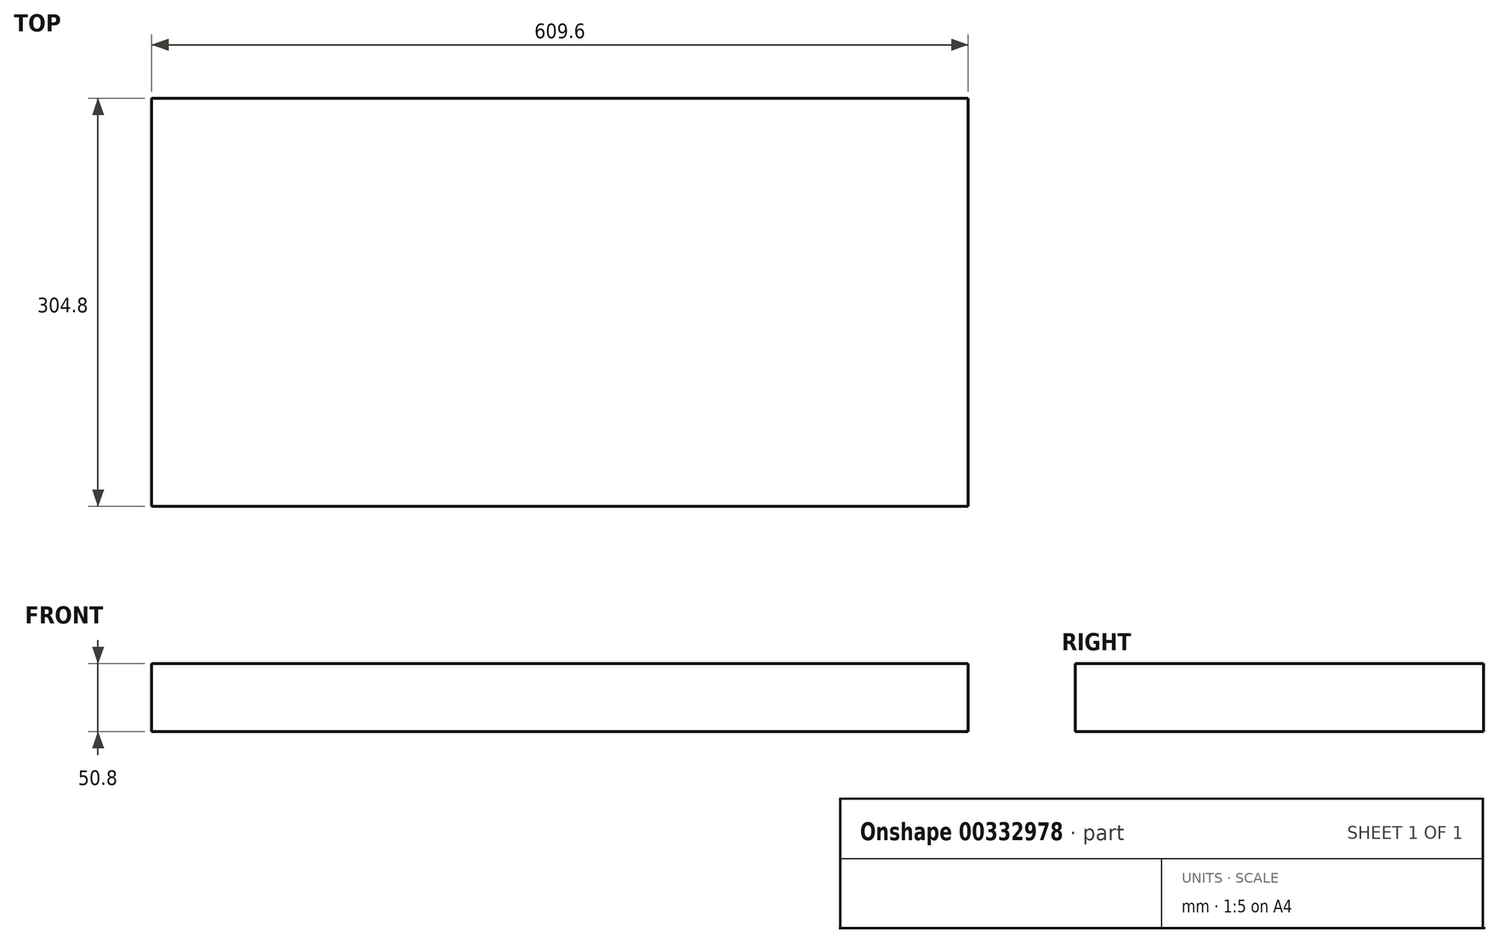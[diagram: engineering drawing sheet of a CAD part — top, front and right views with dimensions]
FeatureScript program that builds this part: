
annotation { "Feature Type Name" : "Feature", "Feature Type Description" : "" }
export const myFeature = defineFeature(function(context is Context, id is Id, definition is map)
    precondition{}
    {
        {
            var Q0;
            Q0=qCreatedBy(makeId("Top.planeOp"),FACE);
            var sketch = newSketch(context, id + "F0", { "sketchPlane" : qUnion([Q0])});
            skLineSegment(sketch, "E0.bottom", {"start": v(304.8, -152.4) * mm, "end": v(-304.8, -152.4) * mm});
            skLineSegment(sketch, "E0.top", {"start": v(304.8, 152.4) * mm, "end": v(-304.8, 152.4) * mm});
            skLineSegment(sketch, "E0.left", {"start": v(304.8, -152.4) * mm, "end": v(304.8, 152.4) * mm});
            skLineSegment(sketch, "E0.right", {"start": v(-304.8, -152.4) * mm, "end": v(-304.8, 152.4) * mm});
            skPoint(sketch, "E0.middle", {"position": v(0, 0) * mm});
            skSolve(sketch);
        }
        {
            var Q0;
            Q0 = qSketchRegion(id + "F0", true);
            extrude(context, id + "F1", {"entities" : qUnion([Q0]), "depth" : 50.8 * mm});
        }
    });
